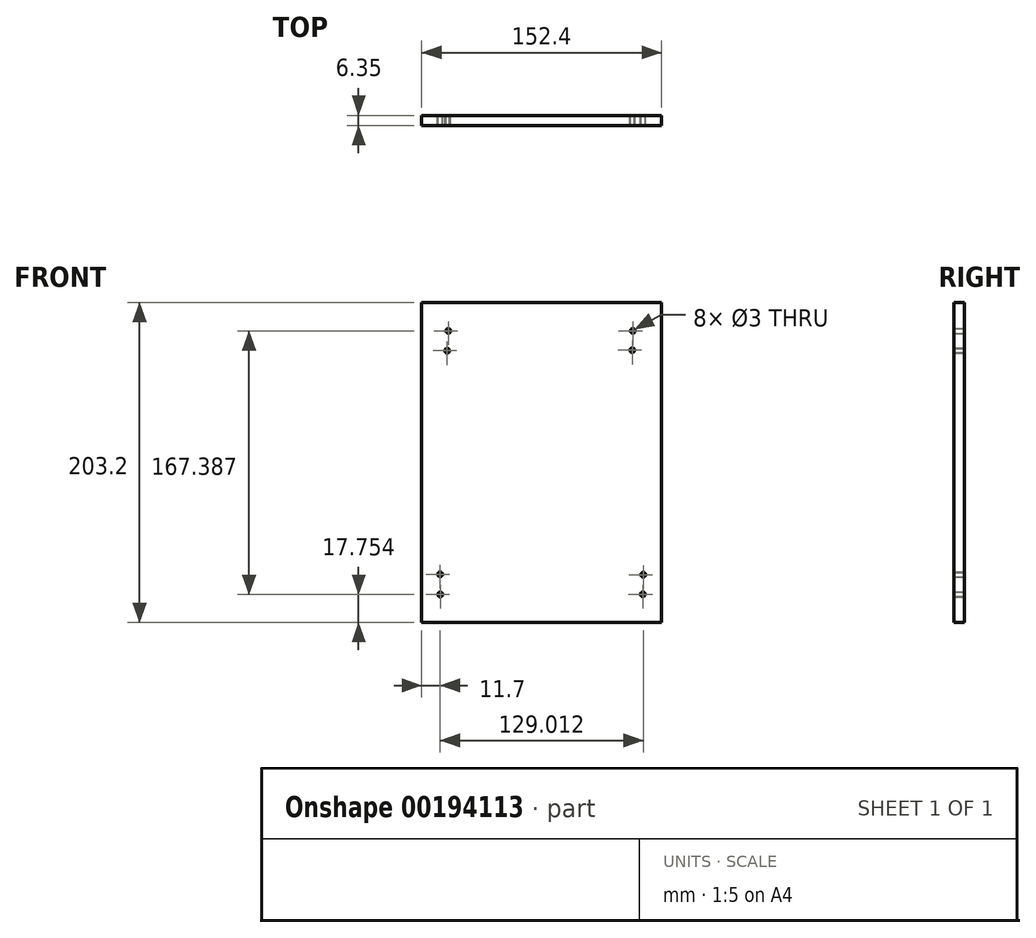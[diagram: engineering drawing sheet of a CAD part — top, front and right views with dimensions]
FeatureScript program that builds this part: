
annotation { "Feature Type Name" : "Feature", "Feature Type Description" : "" }
export const myFeature = defineFeature(function(context is Context, id is Id, definition is map)
    precondition{}
    {
        {
            var Q0;
            Q0=qCreatedBy(makeId("Front.planeOp"),FACE);
            var sketch = newSketch(context, id + "F0", { "sketchPlane" : qUnion([Q0])});
            skLineSegment(sketch, "E0.bottom", {"start": v(-76.2, 101.6) * mm, "end": v(76.2, 101.6) * mm});
            skLineSegment(sketch, "E0.top", {"start": v(-76.2, -101.6) * mm, "end": v(76.2, -101.6) * mm});
            skLineSegment(sketch, "E0.left", {"start": v(-76.2, 101.6) * mm, "end": v(-76.2, -101.6) * mm});
            skLineSegment(sketch, "E0.right", {"start": v(76.2, 101.6) * mm, "end": v(76.2, -101.6) * mm});
            skPoint(sketch, "E0.middle", {"position": v(0, 0) * mm});
            skSolve(sketch);
        }
        {
            var Q0;
            Q0 = qSketchRegion(id + "F0", true);
            extrude(context, id + "F1", {"entities" : qUnion([Q0]), "depth" : 6.35 * mm});
        }
        {
            var Q0;
            Q0=qCreatedBy(makeId("Front.planeOp"),FACE);
            var sketch = newSketch(context, id + "F2", { "sketchPlane" : qUnion([Q0])});
            skCircle(sketch, "E1", {"center": v(-59.29, 83.54) * mm, "radius": 1.5 * mm});
            skCircle(sketch, "E2", {"center": v(-60.03, 70.97) * mm, "radius": 1.5 * mm});
            skCircle(sketch, "E3", {"center": v(57.91, 83.54) * mm, "radius": 1.5 * mm});
            skCircle(sketch, "E4", {"center": v(57.54, 71.34) * mm, "radius": 1.5 * mm});
            skSolve(sketch);
        }
        {
            var Q0;
            Q0 = qSketchRegion(id + "F2", true);
            extrude(context, id + "F3", {"entities" : qUnion([Q0]), "operationType" : NewBodyOperationType.REMOVE, "oppositeDirection" : true, "depth" : 25.4 * mm});
        }
        {
            var Q0;
            Q0 = qSketchRegion(id + "F2", true);
            extrude(context, id + "F4", {"entities" : qUnion([Q0]), "operationType" : NewBodyOperationType.REMOVE, "oppositeDirection" : true, "depth" : 25.4 * mm});
        }
        {
            var Q0;
            Q0 = qSketchRegion(id + "F2", true);
            extrude(context, id + "F5", {"entities" : qUnion([Q0]), "operationType" : NewBodyOperationType.REMOVE, "oppositeDirection" : true, "depth" : 73.66 * mm});
        }
        {
            var Q0;
            Q0 = qSketchRegion(id + "F2", true);
            extrude(context, id + "F6", {"entities" : qUnion([Q0]), "operationType" : NewBodyOperationType.REMOVE, "depth" : 25.4 * mm});
        }
        {
            var Q0;
            Q0=qCreatedBy(makeId("Front.planeOp"),FACE);
            var sketch = newSketch(context, id + "F7", { "sketchPlane" : qUnion([Q0])});
            skCircle(sketch, "E5", {"center": v(64.3, -83.74) * mm, "radius": 1.5 * mm});
            skCircle(sketch, "E6", {"center": v(64.51, -71.3) * mm, "radius": 1.5 * mm});
            skCircle(sketch, "E7", {"center": v(-64.39, -83.85) * mm, "radius": 1.5 * mm});
            skCircle(sketch, "E8", {"center": v(-64.5, -71.09) * mm, "radius": 1.5 * mm});
            skSolve(sketch);
        }
        {
            var Q0;
            Q0 = qSketchRegion(id + "F7", true);
            extrude(context, id + "F8", {"entities" : qUnion([Q0]), "operationType" : NewBodyOperationType.REMOVE, "depth" : 25.4 * mm});
        }
    });
